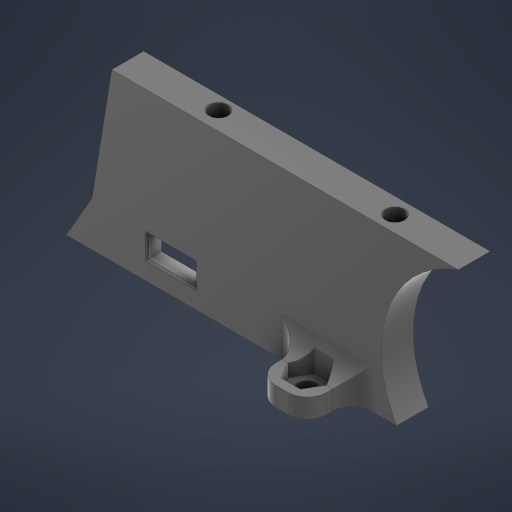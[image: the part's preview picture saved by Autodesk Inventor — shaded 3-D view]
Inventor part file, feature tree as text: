
AUTODESK INVENTOR PART (.ipt)
format: ipt  version: 2024 (Build 280153000, 153)  size: 370,688 bytes
history: native  units: in
note: dims shown in document units (in); Inventor stores cm internally (conversion verified against a paired STEP export)
features: sketch x6, extrude x5, fillet x2, chamfer x1, emboss x1
ambient origin geometry x8: Origin, YZ Plane, XZ Plane, XY Plane, X Axis, Y Axis, Z Axis, Center Point
bodies: Solid1 (feature_tree)
feature tree (15):
  extrude  "Extrusion1"  Depth=0.315in
  extrude  "Extrusion6"  TaperAngle=0.0deg  [1 undecoded]
  chamfer  "Chamfer2"  Distance=0.0984in Angle=45.0deg
  emboss  "Emboss1"
  extrude  "Extrusion8"  Depth=0.1181in TaperAngle=0.0deg
  extrude  "Extrusion9"  Depth=0.0787in TaperAngle=0.0deg
  extrude  "Extrusion10"  Depth=0.1181in
  fillet  "Fillet5"  [1 undecoded]
  fillet  "Fillet6"  [1 undecoded]
  sketch  "Sketch1"  dims[d1=0.1969in d2=0.0in d52=0.315in]
  sketch  "Sketch6"  dims[d53=0.1575in d54=0.0in d55=0.0in d56=0.0984in d57=0.1772in d58=45.0deg]
  sketch  "Sketch9"  dims[d66=0.0394in d67=0.0in d68=0.1181in d69=0.0in]
  sketch  "Sketch10"  dims[d70=0.0787in d71=0.0in d72=0.0787in d73=0.0in]
  sketch  "Sketch11"  dims[d74=0.1181in d75=0.1181in]
  sketch  "Sketch12"
note: 3 required parameter values undecoded (feature->parameter linkage not recoverable at this tier; creation-order binding heuristic only, values carry confidence <= 0.55)
